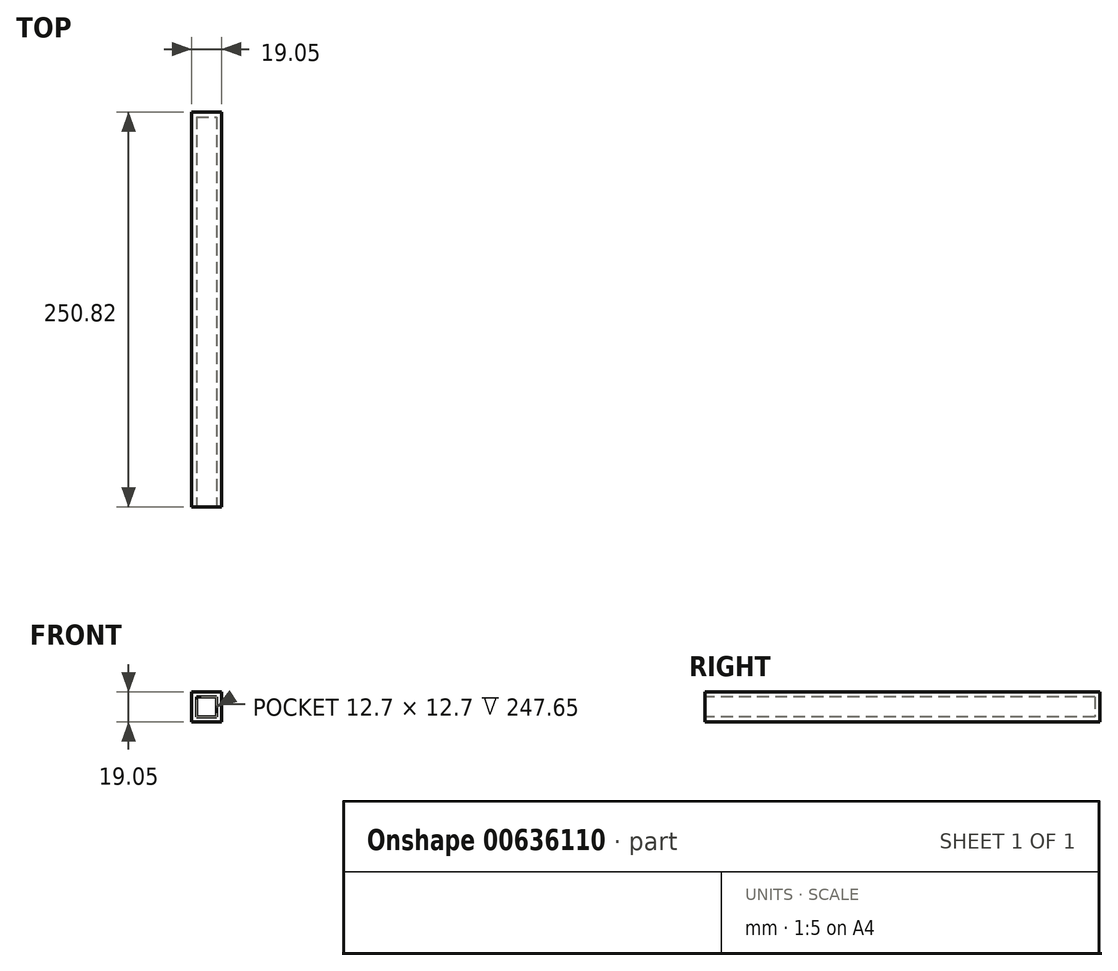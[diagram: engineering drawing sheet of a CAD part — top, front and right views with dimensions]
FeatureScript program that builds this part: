
annotation { "Feature Type Name" : "Feature", "Feature Type Description" : "" }
export const myFeature = defineFeature(function(context is Context, id is Id, definition is map)
    precondition{}
    {
        {
            var Q0;
            Q0=qCreatedBy(makeId("Top.planeOp"),FACE);
            var sketch = newSketch(context, id + "F0", { "sketchPlane" : qUnion([Q0])});
            skLineSegment(sketch, "E0.bottom", {"start": v(-27.4, 267.61) * mm, "end": v(-8.34, 267.61) * mm});
            skLineSegment(sketch, "E0.top", {"start": v(-27.4, 16.79) * mm, "end": v(-8.34, 16.79) * mm});
            skLineSegment(sketch, "E0.left", {"start": v(-27.4, 267.61) * mm, "end": v(-27.4, 16.79) * mm});
            skLineSegment(sketch, "E0.right", {"start": v(-8.34, 267.61) * mm, "end": v(-8.34, 16.79) * mm});
            skSolve(sketch);
        }
        {
            var Q0;
            Q0=makeQuery(id+"F0.imprint","IMPRINT",FACE,{"disambiguationData":[TD([[makeQuery(id+"F0.imprint","IMPRINT",EDGE,{"derivedFrom":sQuery(id+"F0.wireOp",EDGE,"E0.bottom")}),-1.0]])]});
            extrude(context, id + "F1", {"entities" : qUnion([Q0]), "depth" : 19.05 * mm, "offsetDistance" : 25.4 * mm});
        }
        {
            var Q0;
            Q0=makeQuery(id+"F1.opExtrude","SWEPT_FACE",FACE,{"disambiguationData":[OSD([sQuery(id+"F0.wireOp",EDGE,"E0.top")])]});
            shell(context, id + "F2", {"entities" : qUnion([Q0]), "thickness" : 3.17 * mm});
        }
    });
